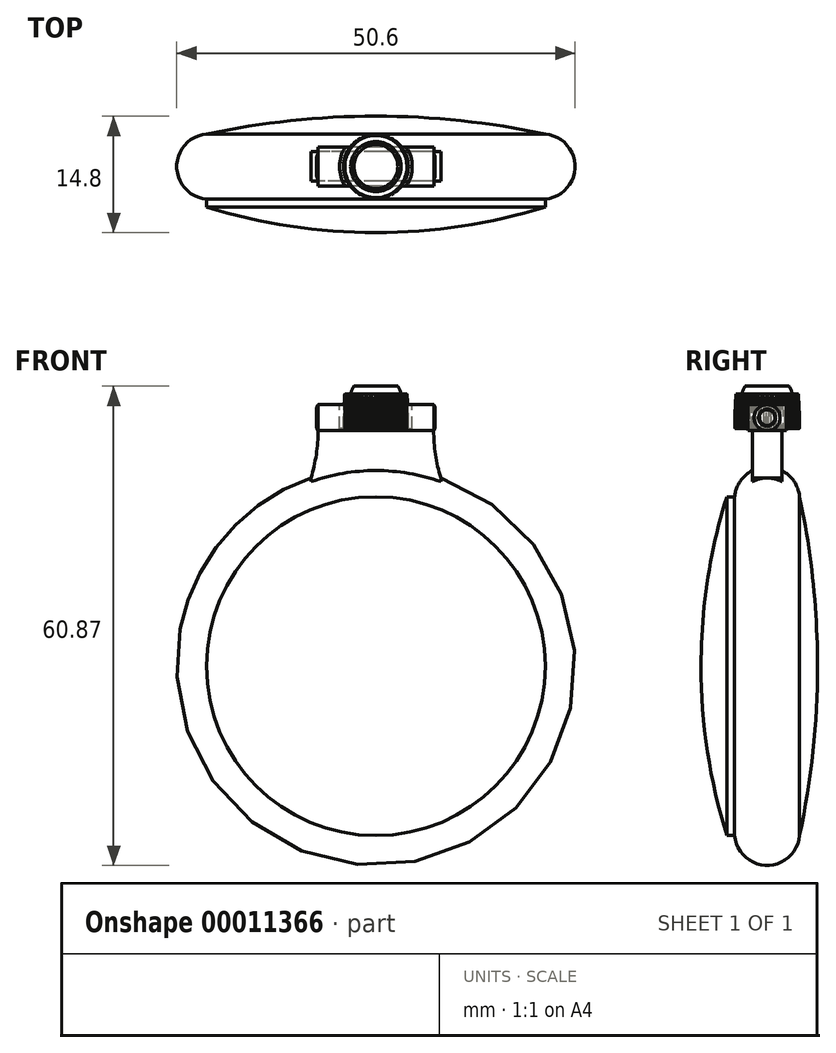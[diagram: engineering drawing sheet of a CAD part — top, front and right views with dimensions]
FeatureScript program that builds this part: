
annotation { "Feature Type Name" : "Feature", "Feature Type Description" : "" }
export const myFeature = defineFeature(function(context is Context, id is Id, definition is map)
    precondition{}
    {
        {
            var Q0;
            Q0=qCreatedBy(makeId("Right.planeOp"),FACE);
            var sketch = newSketch(context, id + "F0", { "sketchPlane" : qUnion([Q0])});
            skPoint(sketch, "E0", {"position": v(-8.4, 0) * mm});
            skPoint(sketch, "E1", {"position": v(0, 25.3) * mm});
            skPoint(sketch, "E2", {"position": v(-4.12, 21.52) * mm});
            skPoint(sketch, "E3", {"position": v(-5.12, 21.52) * mm});
            skLineSegment(sketch, "E4", {"start": v(0, 38.77) * mm, "end": v(0, -36.53) * mm, "construction": true});
            skLineSegment(sketch, "E5", {"start": v(37.65, 0) * mm, "end": v(-34.63, 0) * mm, "construction": true});
            skArc(sketch, "E6", {"start": v(0, 25.3) * mm, "mid": v(-2.8, 24.21) * mm, "end": v(-4.12, 21.52) * mm});
            skArc(sketch, "E7", {"start": v(-5.12, 21.52) * mm, "mid": v(-7.58, 10.88) * mm, "end": v(-8.4, 0) * mm});
            skLineSegment(sketch, "E8.bottom", {"start": v(-8.4, 25.3) * mm, "end": v(0, 25.3) * mm, "construction": true});
            skLineSegment(sketch, "E8.top", {"start": v(-8.4, 0) * mm, "end": v(0, 0) * mm, "construction": true});
            skLineSegment(sketch, "E8.left", {"start": v(-8.4, 25.3) * mm, "end": v(-8.4, 0) * mm, "construction": true});
            skLineSegment(sketch, "E8.right", {"start": v(0, 25.3) * mm, "end": v(0, 0) * mm, "construction": true});
            skLineSegment(sketch, "E9", {"start": v(-4.12, 21.52) * mm, "end": v(-5.12, 21.52) * mm});
            skPoint(sketch, "E10", {"position": v(4.12, 21.52) * mm});
            skPoint(sketch, "E11", {"position": v(6.4, 0) * mm});
            skArc(sketch, "E12", {"start": v(6.4, 0) * mm, "mid": v(5.83, 10.82) * mm, "end": v(4.12, 21.52) * mm});
            skLineSegment(sketch, "E13.bottom", {"start": v(0, 25.3) * mm, "end": v(6.4, 25.3) * mm, "construction": true});
            skLineSegment(sketch, "E13.top", {"start": v(0, 0) * mm, "end": v(6.4, 0) * mm, "construction": true});
            skLineSegment(sketch, "E13.right", {"start": v(6.4, 25.3) * mm, "end": v(6.4, 0) * mm, "construction": true});
            skArc(sketch, "E14", {"start": v(4.12, 21.52) * mm, "mid": v(2.8, 24.21) * mm, "end": v(0, 25.3) * mm});
            skLineSegment(sketch, "E15", {"start": v(-8.4, 0) * mm, "end": v(6.4, 0) * mm});
            skSolve(sketch);
        }
        {
            var Q0;
            Q0=makeQuery(id+"F0.imprint","IMPRINT",FACE,{"disambiguationData":[TD([[makeQuery(id+"F0.imprint","IMPRINT",EDGE,{"derivedFrom":sQuery(id+"F0.wireOp",EDGE,"E6")}),1.0]])]});
            var Q1;
            Q1=sQuery(id+"F0.wireOp",EDGE,"E5");
            revolve(context, id + "F1", {"entities" : qUnion([Q0]), "axis" : qUnion([Q1]), "revolveType" : RevolveType.FULL});
        }
        {
            var Q0;
            Q0=qCreatedBy(makeId("Front.planeOp"),FACE);
            var sketch = newSketch(context, id + "F2", { "sketchPlane" : qUnion([Q0])});
            skCircle(sketch, "E16", {"center": v(0, 0) * mm, "radius": 25.3 * mm, "construction": true});
            skLineSegment(sketch, "E17", {"start": v(-8.25, 23.92) * mm, "end": v(8.25, 23.92) * mm, "construction": true});
            skLineSegment(sketch, "E18.top", {"start": v(-8.25, 29.92) * mm, "end": v(8.25, 29.92) * mm, "construction": true});
            skLineSegment(sketch, "E18.left", {"start": v(-8.25, 23.92) * mm, "end": v(-8.25, 29.92) * mm, "construction": true});
            skLineSegment(sketch, "E18.right", {"start": v(8.25, 23.92) * mm, "end": v(8.25, 29.92) * mm, "construction": true});
            skPoint(sketch, "E19", {"position": v(-7.34, 29.92) * mm});
            skArc(sketch, "E20", {"start": v(-8.25, 23.92) * mm, "mid": v(-7.57, 26.88) * mm, "end": v(-7.34, 29.92) * mm});
            skLineSegment(sketch, "E21.bottom", {"start": v(-7.34, 29.92) * mm, "end": v(7.34, 29.92) * mm, "construction": true});
            skLineSegment(sketch, "E21.top", {"start": v(-7.34, 33.22) * mm, "end": v(7.34, 33.22) * mm, "construction": true});
            skLineSegment(sketch, "E21.left", {"start": v(-7.34, 29.92) * mm, "end": v(-7.34, 33.22) * mm, "construction": true});
            skLineSegment(sketch, "E21.right", {"start": v(7.34, 29.92) * mm, "end": v(7.34, 33.22) * mm, "construction": true});
            skLineSegment(sketch, "E22", {"start": v(0, 0) * mm, "end": v(0, 44.65) * mm, "construction": true});
            skArc(sketch, "E23.0.MirrorCS", {"start": v(8.25, 23.92) * mm, "mid": v(7.57, 26.88) * mm, "end": v(7.34, 29.92) * mm});
            skLineSegment(sketch, "E24", {"start": v(-7.34, 31.57) * mm, "end": v(7.34, 31.57) * mm, "construction": true});
            skLineSegment(sketch, "E25.rect.bottom", {"start": v(7.36, 29.92) * mm, "end": v(-7.36, 29.92) * mm});
            skLineSegment(sketch, "E25.rect.top", {"start": v(7.36, 33.22) * mm, "end": v(-7.36, 33.22) * mm});
            skLineSegment(sketch, "E25.rect.left", {"start": v(7.36, 29.92) * mm, "end": v(7.36, 33.22) * mm});
            skLineSegment(sketch, "E25.rect.right", {"start": v(-7.36, 29.92) * mm, "end": v(-7.36, 33.22) * mm});
            skPoint(sketch, "E25.rect.middle", {"position": v(0, 31.57) * mm});
            skLineSegment(sketch, "E26", {"start": v(-8.25, 23.92) * mm, "end": v(8.25, 23.92) * mm});
            skSolve(sketch);
        }
        {
            var Q0;
            {var subQ2=sQuery(id+"F2.wireOp",EDGE,"E20");Q0=makeQuery(id+"F2.imprint","IMPRINT",FACE,{"disambiguationData":[TD([[makeQuery(id+"F2.imprint","IMPRINT",EDGE,{"derivedFrom":subQ2}),-1.0]])]});}
            extrude(context, id + "F3", {"entities" : qUnion([Q0]), "operationType" : NewBodyOperationType.ADD, "endBound" : BoundingType.SYMMETRIC, "depth" : 3.75 * mm});
        }
        {
            var Q0;
            {var subQ0=sQuery(id+"F2.wireOp",EDGE,"E26");var subQ1=makeQuery(id+"F3.opExtrude","SWEPT_FACE",FACE,{"disambiguationData":[OSD([subQ0])]});var subQ2=sQuery(id+"F2.wireOp",EDGE,"E23.0.MirrorCS");Q0=makeQuery(id+"F3.boolean.opBoolean","SPLIT",FACE,{"disambiguationData":[TD([makeQuery(id+"F1.opRevolve","SWEPT_FACE",FACE,{"disambiguationData":[OSD([sQuery(id+"F0.wireOp",EDGE,"E6"),sQuery(id+"F0.wireOp",EDGE,"E14")])]}),makeQuery(id+"F3.opExtrude","CAP_FACE",FACE,{"disambiguationData":[OSD([sQuery(id+"F2.wireOp",EDGE,"E20"),subQ2,sQuery(id+"F2.wireOp",EDGE,"E25.rect.bottom"),subQ0])],"isStart":false}),makeQuery(id+"F3.opExtrude","SWEPT_FACE",FACE,{"disambiguationData":[OSD([subQ2])]}),subQ1])],"derivedFrom":subQ1});}
            var Q1;
            {var subQ0=sQuery(id+"F2.wireOp",EDGE,"E26");var subQ1=makeQuery(id+"F3.opExtrude","SWEPT_FACE",FACE,{"disambiguationData":[OSD([subQ0])]});var subQ2=sQuery(id+"F2.wireOp",EDGE,"E23.0.MirrorCS");Q1=makeQuery(id+"F3.boolean.opBoolean","SPLIT",FACE,{"disambiguationData":[TD([makeQuery(id+"F1.opRevolve","SWEPT_FACE",FACE,{"disambiguationData":[OSD([sQuery(id+"F0.wireOp",EDGE,"E6"),sQuery(id+"F0.wireOp",EDGE,"E14")])]}),makeQuery(id+"F3.opExtrude","CAP_FACE",FACE,{"disambiguationData":[OSD([sQuery(id+"F2.wireOp",EDGE,"E20"),subQ2,sQuery(id+"F2.wireOp",EDGE,"E25.rect.bottom"),subQ0])],"isStart":true}),makeQuery(id+"F3.opExtrude","SWEPT_FACE",FACE,{"disambiguationData":[OSD([subQ2])]}),subQ1])],"derivedFrom":subQ1});}
            var Q2;
            {var subQ0=sQuery(id+"F2.wireOp",EDGE,"E26");var subQ1=makeQuery(id+"F3.opExtrude","SWEPT_FACE",FACE,{"disambiguationData":[OSD([subQ0])]});var subQ2=sQuery(id+"F2.wireOp",EDGE,"E20");Q2=makeQuery(id+"F3.boolean.opBoolean","SPLIT",FACE,{"disambiguationData":[TD([makeQuery(id+"F1.opRevolve","SWEPT_FACE",FACE,{"disambiguationData":[OSD([sQuery(id+"F0.wireOp",EDGE,"E6"),sQuery(id+"F0.wireOp",EDGE,"E14")])]}),makeQuery(id+"F3.opExtrude","SWEPT_FACE",FACE,{"disambiguationData":[OSD([subQ2])]}),makeQuery(id+"F3.opExtrude","CAP_FACE",FACE,{"disambiguationData":[OSD([subQ2,sQuery(id+"F2.wireOp",EDGE,"E23.0.MirrorCS"),sQuery(id+"F2.wireOp",EDGE,"E25.rect.bottom"),subQ0])],"isStart":false}),subQ1])],"derivedFrom":subQ1});}
            var Q3;
            {var subQ0=sQuery(id+"F2.wireOp",EDGE,"E26");var subQ1=makeQuery(id+"F3.opExtrude","SWEPT_FACE",FACE,{"disambiguationData":[OSD([subQ0])]});var subQ2=sQuery(id+"F2.wireOp",EDGE,"E20");Q3=makeQuery(id+"F3.boolean.opBoolean","SPLIT",FACE,{"disambiguationData":[TD([makeQuery(id+"F1.opRevolve","SWEPT_FACE",FACE,{"disambiguationData":[OSD([sQuery(id+"F0.wireOp",EDGE,"E6"),sQuery(id+"F0.wireOp",EDGE,"E14")])]}),makeQuery(id+"F3.opExtrude","SWEPT_FACE",FACE,{"disambiguationData":[OSD([subQ2])]}),makeQuery(id+"F3.opExtrude","CAP_FACE",FACE,{"disambiguationData":[OSD([subQ2,sQuery(id+"F2.wireOp",EDGE,"E23.0.MirrorCS"),sQuery(id+"F2.wireOp",EDGE,"E25.rect.bottom"),subQ0])],"isStart":true}),subQ1])],"derivedFrom":subQ1});}
            extrude(context, id + "F4", {"entities" : qUnion([Q0, Q1, Q2, Q3]), "operationType" : NewBodyOperationType.ADD, "depth" : 5 * mm});
        }
        {
            var Q0;
            Q0=makeQuery(id+"F2.imprint","IMPRINT",FACE,{"disambiguationData":[TD([[makeQuery(id+"F2.imprint","IMPRINT",EDGE,{"derivedFrom":sQuery(id+"F2.wireOp",EDGE,"E25.rect.top")}),1.0]])]});
            extrude(context, id + "F5", {"entities" : qUnion([Q0]), "operationType" : NewBodyOperationType.ADD, "endBound" : BoundingType.SYMMETRIC, "depth" : 4.9 * mm});
        }
        {
            var Q0;
            Q0=makeQuery(id+"F5.opExtrude","SWEPT_FACE",FACE,{"disambiguationData":[OSD([sQuery(id+"F2.wireOp",EDGE,"E25.rect.top")])]});
            var sketch = newSketch(context, id + "F6", { "sketchPlane" : qUnion([Q0])});
            skCircle(sketch, "E27", {"center": v(0, 0) * mm, "radius": 4.62 * mm});
            skSolve(sketch);
        }
        {
            var Q0;
            {var subQ0=makeQuery(id+"F5.opExtrude","CAP_EDGE",EDGE,{"disambiguationData":[OSD([sQuery(id+"F2.wireOp",EDGE,"E25.rect.top")])],"isStart":true});var subQ1=sQuery(id+"F6.wireOp",EDGE,"E27");var subQ3=makeQuery(id+"F6.imprint","INTERSECT",VERTEX,{"disambiguationData":[OD(0.0)],"derivedFrom":[subQ0,subQ1]});Q0=makeQuery(id+"F6.imprint","IMPRINT",FACE,{"disambiguationData":[TD([[makeQuery(id+"F6.imprint","IMPRINT",EDGE,{"disambiguationData":[TD([[subQ3,1.0]])],"derivedFrom":subQ1}),1.0]])]});}
            var Q1;
            {var subQ0=sQuery(id+"F2.wireOp",EDGE,"E25.rect.top");var subQ2=sQuery(id+"F6.wireOp",EDGE,"E27");var subQ5=makeQuery(id+"F5.opExtrude","CAP_EDGE",EDGE,{"disambiguationData":[OSD([subQ0])],"isStart":true});var subQ7=makeQuery(id+"F6.imprint","INTERSECT",VERTEX,{"disambiguationData":[OD(0.0)],"derivedFrom":[subQ5,subQ2]});Q1=makeQuery(id+"F6.imprint","IMPRINT",FACE,{"disambiguationData":[TD([[makeQuery(id+"F6.imprint","IMPRINT",EDGE,{"disambiguationData":[TD([[subQ7,-1.0]])],"derivedFrom":subQ2}),1.0]])]});}
            var Q2;
            {var subQ0=makeQuery(id+"F5.opExtrude","CAP_EDGE",EDGE,{"disambiguationData":[OSD([sQuery(id+"F2.wireOp",EDGE,"E25.rect.top")])],"isStart":false});var subQ1=sQuery(id+"F6.wireOp",EDGE,"E27");var subQ3=makeQuery(id+"F6.imprint","INTERSECT",VERTEX,{"disambiguationData":[OD(0.0)],"derivedFrom":[subQ0,subQ1]});Q2=makeQuery(id+"F6.imprint","IMPRINT",FACE,{"disambiguationData":[TD([[makeQuery(id+"F6.imprint","IMPRINT",EDGE,{"disambiguationData":[TD([[subQ3,-1.0]])],"derivedFrom":subQ1}),1.0]])]});}
            extrude(context, id + "F7", {"entities" : qUnion([Q0, Q1, Q2]), "operationType" : NewBodyOperationType.REMOVE, "oppositeDirection" : true, "depth" : 3 * mm});
        }
        {
            var Q0;
            Q0=makeQuery(id+"F7.boolean.opBoolean","COPY",FACE,{"derivedFrom":makeQuery(id+"F7.opExtrude","CAP_FACE",FACE,{"disambiguationData":[OSD([sQuery(id+"F6.wireOp",EDGE,"E27")])],"isStart":false})});
            var sketch = newSketch(context, id + "F8", { "sketchPlane" : qUnion([Q0])});
            skCircle(sketch, "E28", {"center": v(0, 0) * mm, "radius": 4.12 * mm});
            skCircle(sketch, "E29", {"center": v(0, 4.12) * mm, "radius": 0.16 * mm});
            skCircle(sketch, "E30.1.0", {"center": v(0.64, 4.06) * mm, "radius": 0.16 * mm});
            skCircle(sketch, "E30.2.0", {"center": v(1.27, 3.91) * mm, "radius": 0.16 * mm});
            skCircle(sketch, "E30.3.0", {"center": v(1.87, 3.67) * mm, "radius": 0.16 * mm});
            skCircle(sketch, "E30.4.0", {"center": v(2.42, 3.33) * mm, "radius": 0.16 * mm});
            skCircle(sketch, "E30.5.0", {"center": v(2.9, 2.9) * mm, "radius": 0.16 * mm});
            skCircle(sketch, "E30.6.0", {"center": v(3.33, 2.42) * mm, "radius": 0.16 * mm});
            skCircle(sketch, "E30.7.0", {"center": v(3.67, 1.87) * mm, "radius": 0.16 * mm});
            skCircle(sketch, "E30.8.0", {"center": v(3.91, 1.27) * mm, "radius": 0.16 * mm});
            skCircle(sketch, "E30.9.0", {"center": v(4.06, 0.64) * mm, "radius": 0.16 * mm});
            skCircle(sketch, "E30.10.0", {"center": v(4.12, 0) * mm, "radius": 0.16 * mm});
            skCircle(sketch, "E30.11.0", {"center": v(4.06, -0.64) * mm, "radius": 0.16 * mm});
            skCircle(sketch, "E30.12.0", {"center": v(3.91, -1.27) * mm, "radius": 0.16 * mm});
            skCircle(sketch, "E30.13.0", {"center": v(3.67, -1.87) * mm, "radius": 0.16 * mm});
            skCircle(sketch, "E30.14.0", {"center": v(3.33, -2.42) * mm, "radius": 0.16 * mm});
            skCircle(sketch, "E30.15.0", {"center": v(2.9, -2.9) * mm, "radius": 0.16 * mm});
            skCircle(sketch, "E30.16.0", {"center": v(2.42, -3.33) * mm, "radius": 0.16 * mm});
            skCircle(sketch, "E30.17.0", {"center": v(1.87, -3.67) * mm, "radius": 0.16 * mm});
            skCircle(sketch, "E30.18.0", {"center": v(1.27, -3.91) * mm, "radius": 0.16 * mm});
            skCircle(sketch, "E30.19.0", {"center": v(0.64, -4.06) * mm, "radius": 0.16 * mm});
            skCircle(sketch, "E30.20.0", {"center": v(0, -4.12) * mm, "radius": 0.16 * mm});
            skCircle(sketch, "E30.21.0", {"center": v(-0.64, -4.06) * mm, "radius": 0.16 * mm});
            skCircle(sketch, "E30.22.0", {"center": v(-1.27, -3.91) * mm, "radius": 0.16 * mm});
            skCircle(sketch, "E30.23.0", {"center": v(-1.87, -3.67) * mm, "radius": 0.16 * mm});
            skCircle(sketch, "E30.24.0", {"center": v(-2.42, -3.33) * mm, "radius": 0.16 * mm});
            skCircle(sketch, "E30.25.0", {"center": v(-2.9, -2.9) * mm, "radius": 0.16 * mm});
            skCircle(sketch, "E30.26.0", {"center": v(-3.33, -2.42) * mm, "radius": 0.16 * mm});
            skCircle(sketch, "E30.27.0", {"center": v(-3.67, -1.87) * mm, "radius": 0.16 * mm});
            skCircle(sketch, "E30.28.0", {"center": v(-3.91, -1.27) * mm, "radius": 0.16 * mm});
            skCircle(sketch, "E30.29.0", {"center": v(-4.06, -0.64) * mm, "radius": 0.16 * mm});
            skCircle(sketch, "E30.30.0", {"center": v(-4.12, 0) * mm, "radius": 0.16 * mm});
            skCircle(sketch, "E30.31.0", {"center": v(-4.06, 0.64) * mm, "radius": 0.16 * mm});
            skCircle(sketch, "E30.32.0", {"center": v(-3.91, 1.27) * mm, "radius": 0.16 * mm});
            skCircle(sketch, "E30.33.0", {"center": v(-3.67, 1.87) * mm, "radius": 0.16 * mm});
            skCircle(sketch, "E30.34.0", {"center": v(-3.33, 2.42) * mm, "radius": 0.16 * mm});
            skCircle(sketch, "E30.35.0", {"center": v(-2.9, 2.9) * mm, "radius": 0.16 * mm});
            skCircle(sketch, "E30.36.0", {"center": v(-2.42, 3.33) * mm, "radius": 0.16 * mm});
            skCircle(sketch, "E30.37.0", {"center": v(-1.87, 3.67) * mm, "radius": 0.16 * mm});
            skCircle(sketch, "E30.38.0", {"center": v(-1.27, 3.91) * mm, "radius": 0.16 * mm});
            skCircle(sketch, "E30.39.0", {"center": v(-0.64, 4.06) * mm, "radius": 0.16 * mm});
            skLineSegment(sketch, "E30.anchor1", {"start": v(0, 0) * mm, "end": v(0, 4.12) * mm, "construction": true});
            skLineSegment(sketch, "E30.anchor2", {"start": v(0, 0) * mm, "end": v(-0.64, 4.06) * mm, "construction": true});
            skSolve(sketch);
        }
        {
            var Q0;
            {var subQ1=sQuery(id+"F8.wireOp",EDGE,"E30.26.0");var subQ6=sQuery(id+"F8.wireOp",EDGE,"E28");var subQ9=makeQuery(id+"F8.imprint","INTERSECT",VERTEX,{"disambiguationData":[OD(0.0)],"derivedFrom":[subQ6,subQ1]});Q0=makeQuery(id+"F8.imprint","IMPRINT",FACE,{"disambiguationData":[TD([[makeQuery(id+"F8.imprint","IMPRINT",EDGE,{"disambiguationData":[TD([[subQ9,-1.0]])],"derivedFrom":subQ6}),1.0]])]});}
            var Q1;
            {var subQ11=sQuery(id+"F8.wireOp",EDGE,"E28");var subQ36=sQuery(id+"F8.wireOp",EDGE,"E30.9.0");var subQ57=makeQuery(id+"F8.imprint","INTERSECT",VERTEX,{"disambiguationData":[OD(0.0)],"derivedFrom":[subQ11,subQ36]});Q1=makeQuery(id+"F8.imprint","IMPRINT",FACE,{"disambiguationData":[TD([[makeQuery(id+"F8.imprint","IMPRINT",EDGE,{"disambiguationData":[TD([[subQ57,1.0]])],"derivedFrom":subQ11}),1.0]])]});}
            var Q2;
            {var subQ3=sQuery(id+"F8.wireOp",EDGE,"E30.6.0");var subQ6=sQuery(id+"F8.wireOp",EDGE,"E28");var subQ14=makeQuery(id+"F8.imprint","INTERSECT",VERTEX,{"disambiguationData":[OD(0.0)],"derivedFrom":[subQ6,subQ3]});Q2=makeQuery(id+"F8.imprint","IMPRINT",FACE,{"disambiguationData":[TD([[makeQuery(id+"F8.imprint","IMPRINT",EDGE,{"disambiguationData":[TD([[subQ14,-1.0]])],"derivedFrom":subQ6}),1.0]])]});}
            extrude(context, id + "F9", {"entities" : qUnion([Q0, Q1, Q2]), "operationType" : NewBodyOperationType.ADD, "depth" : 5.35 * mm});
        }
        {
            var Q0;
            Q0=qCreatedBy(makeId("Right.planeOp"),FACE);
            var sketch = newSketch(context, id + "F10", { "sketchPlane" : qUnion([Q0])});
            skPoint(sketch, "E31.0", {"position": v(-4.12, 30.09) * mm});
            skPoint(sketch, "E32.0", {"position": v(3.02, 30.22) * mm});
            skPoint(sketch, "E33.0", {"position": v(3.02, 35.57) * mm});
            skPoint(sketch, "E34.0", {"position": v(-4.12, 35.57) * mm});
            skLineSegment(sketch, "E35.bottom", {"start": v(-4.12, 35.57) * mm, "end": v(3.02, 35.57) * mm, "construction": true});
            skLineSegment(sketch, "E35.top", {"start": v(-4.11, 30.22) * mm, "end": v(3.02, 30.22) * mm, "construction": true});
            skLineSegment(sketch, "E35.left", {"start": v(-4.12, 35.57) * mm, "end": v(-4.11, 30.22) * mm, "construction": true});
            skLineSegment(sketch, "E35.right", {"start": v(3.02, 35.57) * mm, "end": v(3.02, 30.22) * mm, "construction": true});
            skLineSegment(sketch, "E36", {"start": v(0, 35.57) * mm, "end": v(0, 30.22) * mm, "construction": true});
            skLineSegment(sketch, "E37", {"start": v(-3.95, 34.57) * mm, "end": v(3.02, 34.57) * mm});
            skPoint(sketch, "E38", {"position": v(-3.19, 34.57) * mm});
            skPoint(sketch, "E39", {"position": v(-2.8, 35.57) * mm});
            skArc(sketch, "E40", {"start": v(-2.8, 35.57) * mm, "mid": v(-3.05, 35.09) * mm, "end": v(-3.19, 34.57) * mm});
            skPoint(sketch, "E41", {"position": v(-3.95, 34.57) * mm});
            skArc(sketch, "E42", {"start": v(-3.95, 34.57) * mm, "mid": v(-4.07, 32.33) * mm, "end": v(-4.12, 30.09) * mm});
            skLineSegment(sketch, "E43", {"start": v(-2.8, 35.57) * mm, "end": v(-4.12, 35.57) * mm});
            skLineSegment(sketch, "E44", {"start": v(-4.12, 35.57) * mm, "end": v(-4.12, 30.09) * mm});
            skSolve(sketch);
        }
        {
            var Q0;
            Q0 = qSketchRegion(id + "F10", true);
            var Q1;
            Q1=sQuery(id+"F10.wireOp",EDGE,"E36");
            revolve(context, id + "F11", {"operationType" : NewBodyOperationType.REMOVE, "entities" : qUnion([Q0]), "axis" : qUnion([Q1]), "revolveType" : RevolveType.FULL, "oppositeDirection" : true});
        }
        {
            var Q0;
            Q0=makeQuery(id+"F5.opExtrude","SWEPT_FACE",FACE,{"disambiguationData":[OSD([sQuery(id+"F2.wireOp",EDGE,"E25.rect.right")])]});
            var sketch = newSketch(context, id + "F12", { "sketchPlane" : qUnion([Q0])});
            skLineSegment(sketch, "E45", {"start": v(0, 29.92) * mm, "end": v(0, 33.22) * mm, "construction": true});
            skPoint(sketch, "E46", {"position": v(0, 31.57) * mm});
            skSolve(sketch);
        }
        {
            var Q0;
            Q0=sQuery(id+"F12.wireOp",EDGE,"E45");
            var Q1;
            Q1=sQuery(id+"F12.wireOp",VERTEX,"E46");
            cPlane(context, id + "F13", {"entities" : qUnion([Q0, Q1]), "cplaneType" : CPlaneType.LINE_POINT, "offset" : 150 * mm, "width" : 150 * mm, "height" : 150 * mm});
        }
        {
            var Q0;
            Q0=qCreatedBy(id+"F13.planeOp",FACE);
            var sketch = newSketch(context, id + "F14", { "sketchPlane" : qUnion([Q0])});
            skPoint(sketch, "E47.0", {"position": v(-7.36, 0) * mm});
            skLineSegment(sketch, "E48", {"start": v(-7.36, 0) * mm, "end": v(-7.4, 0) * mm});
            skLineSegment(sketch, "E49", {"start": v(-7.4, 0) * mm, "end": v(-7.4, -1) * mm});
            skLineSegment(sketch, "E50", {"start": v(-7.4, -1) * mm, "end": v(-7.54, -1.1) * mm});
            skLineSegment(sketch, "E51.0", {"start": v(-7.36, -2.45) * mm, "end": v(-7.36, 2.45) * mm});
            skArc(sketch, "E52", {"start": v(-7.54, -1.1) * mm, "mid": v(-7.48, -1.39) * mm, "end": v(-7.36, -1.66) * mm});
            skLineSegment(sketch, "E53.0", {"start": v(7.36, -2.45) * mm, "end": v(7.36, 2.45) * mm});
            skLineSegment(sketch, "E54", {"start": v(7.36, 0) * mm, "end": v(-7.36, 0) * mm, "construction": true});
            skLineSegment(sketch, "E55", {"start": v(0, 0) * mm, "end": v(0, -2.4) * mm, "construction": true});
            skLineSegment(sketch, "E56.1.MirrorCS", {"start": v(7.36, 0) * mm, "end": v(7.4, 0) * mm});
            skLineSegment(sketch, "E56.2.MirrorCS", {"start": v(7.4, -1) * mm, "end": v(7.54, -1.1) * mm});
            skLineSegment(sketch, "E56.3.MirrorCS", {"start": v(7.4, 0) * mm, "end": v(7.4, -1) * mm});
            skArc(sketch, "E56.4.MirrorCS", {"start": v(7.54, -1.1) * mm, "mid": v(7.48, -1.39) * mm, "end": v(7.36, -1.66) * mm});
            skSolve(sketch);
        }
        {
            var Q0;
            {var subQ2=sQuery(id+"F14.wireOp",EDGE,"E48");Q0=makeQuery(id+"F14.imprint","IMPRINT",FACE,{"disambiguationData":[TD([[makeQuery(id+"F14.imprint","IMPRINT",EDGE,{"derivedFrom":subQ2}),1.0]])]});}
            var Q1;
            {var subQ1=sQuery(id+"F14.wireOp",EDGE,"E56.1.MirrorCS");Q1=makeQuery(id+"F14.imprint","IMPRINT",FACE,{"disambiguationData":[TD([[makeQuery(id+"F14.imprint","IMPRINT",EDGE,{"derivedFrom":subQ1}),-1.0]])]});}
            var Q2;
            Q2=sQuery(id+"F14.wireOp",EDGE,"E48");
            revolve(context, id + "F15", {"operationType" : NewBodyOperationType.ADD, "entities" : qUnion([Q0, Q1]), "axis" : qUnion([Q2]), "revolveType" : RevolveType.FULL});
        }
    });
